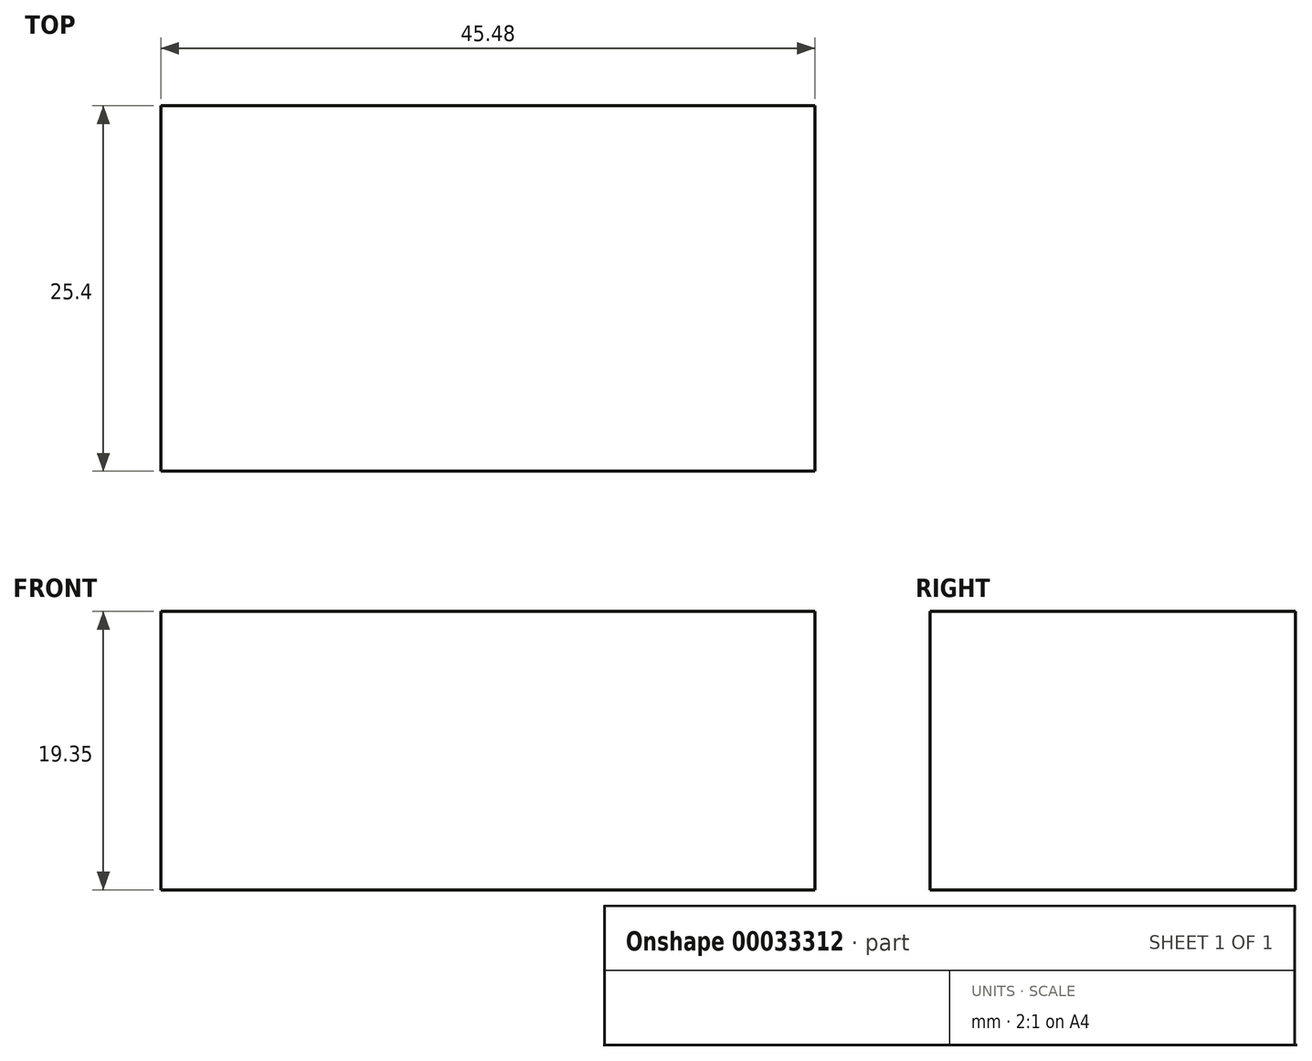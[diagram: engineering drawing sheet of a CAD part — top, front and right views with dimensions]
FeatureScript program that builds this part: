
annotation { "Feature Type Name" : "Feature", "Feature Type Description" : "" }
export const myFeature = defineFeature(function(context is Context, id is Id, definition is map)
    precondition{}
    {
        {
            var Q0;
            Q0=qCreatedBy(makeId("Front.planeOp"),FACE);
            var sketch = newSketch(context, id + "F0", { "sketchPlane" : qUnion([Q0])});
            skLineSegment(sketch, "E0.bottom", {"start": v(-46.83, 7.06) * mm, "end": v(-1.35, 7.06) * mm});
            skLineSegment(sketch, "E0.top", {"start": v(-46.83, 26.41) * mm, "end": v(-1.35, 26.41) * mm});
            skLineSegment(sketch, "E0.left", {"start": v(-46.83, 7.06) * mm, "end": v(-46.83, 26.41) * mm});
            skLineSegment(sketch, "E0.right", {"start": v(-1.35, 7.06) * mm, "end": v(-1.35, 26.41) * mm});
            skSolve(sketch);
        }
        {
            var Q0;
            Q0 = qSketchRegion(id + "F0", true);
            extrude(context, id + "F1", {"entities" : qUnion([Q0]), "depth" : 25.4 * mm});
        }
    });
